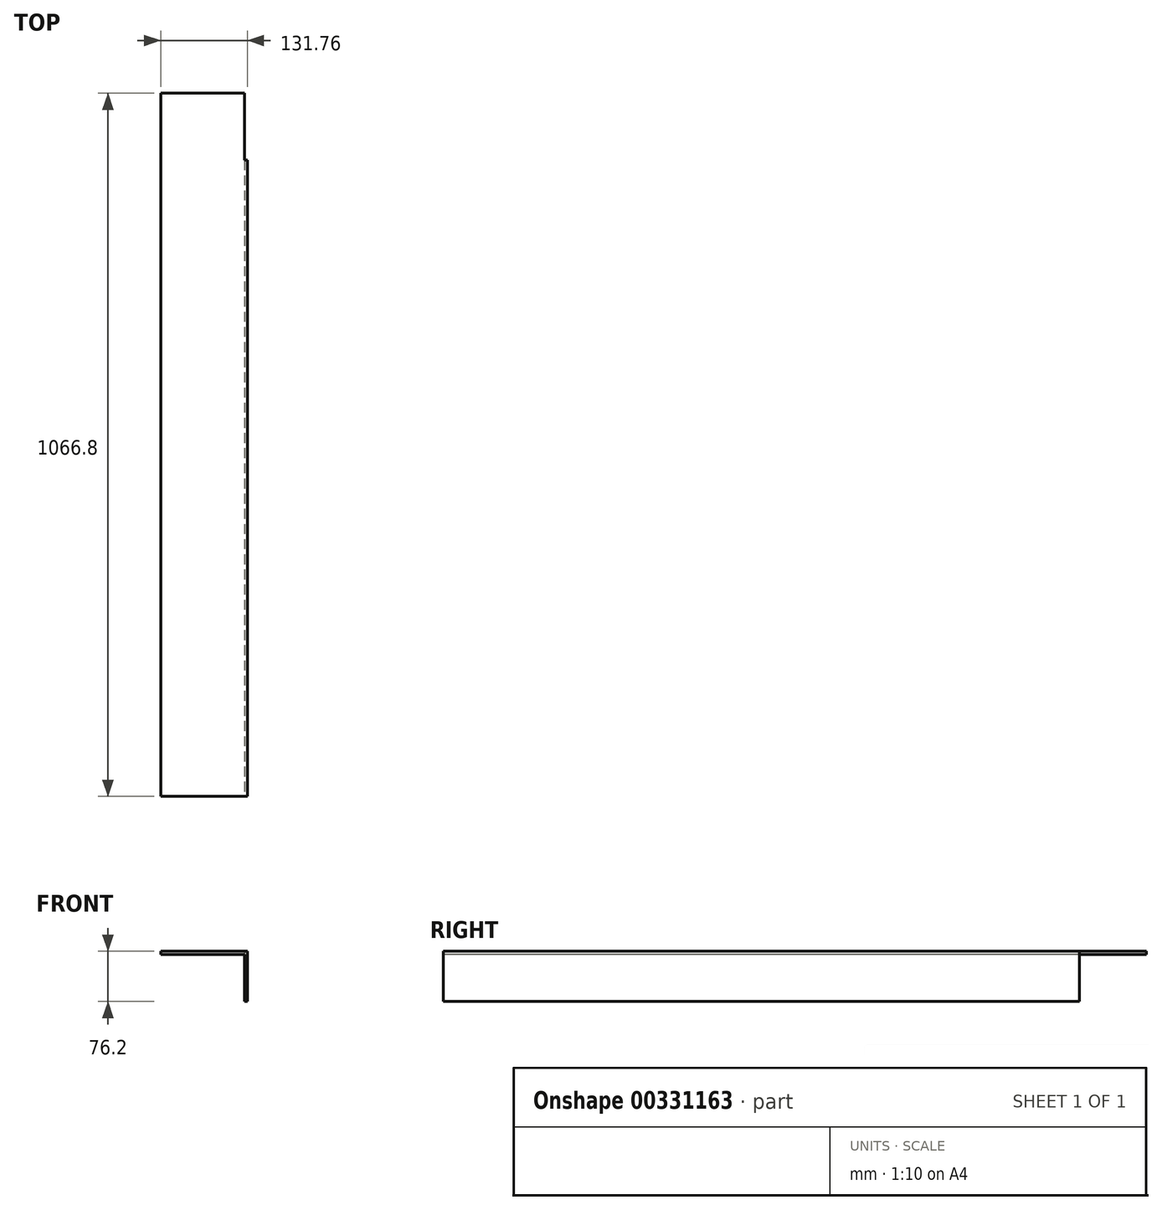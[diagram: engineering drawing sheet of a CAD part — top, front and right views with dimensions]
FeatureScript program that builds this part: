
annotation { "Feature Type Name" : "Feature", "Feature Type Description" : "" }
export const myFeature = defineFeature(function(context is Context, id is Id, definition is map)
    precondition{}
    {
        {
            var Q0;
            Q0=qCreatedBy(makeId("Top.planeOp"),FACE);
            var sketch = newSketch(context, id + "F0", { "sketchPlane" : qUnion([Q0])});
            skLineSegment(sketch, "E0.bottom", {"start": v(63.5, 533.4) * mm, "end": v(-63.5, 533.4) * mm});
            skLineSegment(sketch, "E0.top", {"start": v(63.5, -533.4) * mm, "end": v(-63.5, -533.4) * mm});
            skLineSegment(sketch, "E0.left", {"start": v(63.5, -381) * mm, "end": v(63.5, -533.4) * mm});
            skLineSegment(sketch, "E0.right", {"start": v(-63.5, 533.4) * mm, "end": v(-63.5, -533.4) * mm});
            skPoint(sketch, "E0.middle", {"position": v(0, 0) * mm});
            skLineSegment(sketch, "E1", {"start": v(63.5, 533.4) * mm, "end": v(63.5, -381) * mm});
            skSolve(sketch);
        }
        {
            var Q0;
            Q0 = qSketchRegion(id + "F0", true);
            extrude(context, id + "F1", {"entities" : qUnion([Q0]), "depth" : 4.76 * mm});
        }
        {
            var Q0;
            Q0=makeQuery(id+"F1.opExtrude","SWEPT_FACE",FACE,{"disambiguationData":[OSD([sQuery(id+"F0.wireOp",EDGE,"E0.left"),sQuery(id+"F0.wireOp",EDGE,"E1")])]});
            var sketch = newSketch(context, id + "F2", { "sketchPlane" : qUnion([Q0])});
            skLineSegment(sketch, "E2.bottom", {"start": v(-533.4, 4.76) * mm, "end": v(431.8, 4.76) * mm});
            skLineSegment(sketch, "E2.top", {"start": v(-533.4, -71.44) * mm, "end": v(431.8, -71.44) * mm});
            skLineSegment(sketch, "E2.left", {"start": v(-533.4, 4.76) * mm, "end": v(-533.4, -71.44) * mm});
            skLineSegment(sketch, "E2.right", {"start": v(431.8, 4.76) * mm, "end": v(431.8, -71.44) * mm});
            skSolve(sketch);
        }
        {
            var Q0;
            Q0 = qSketchRegion(id + "F2", true);
            extrude(context, id + "F3", {"entities" : qUnion([Q0]), "operationType" : NewBodyOperationType.ADD, "depth" : 4.76 * mm});
        }
    });
